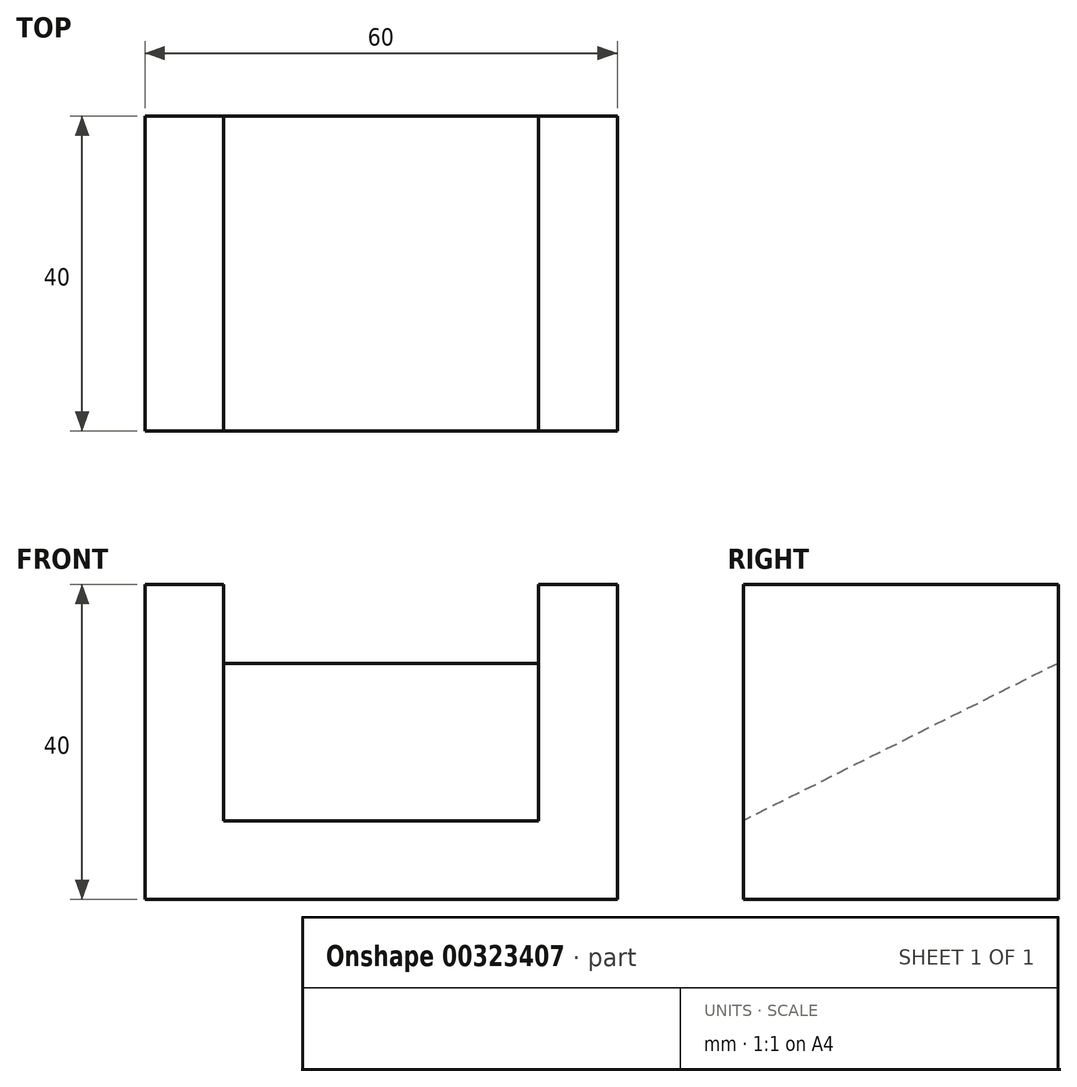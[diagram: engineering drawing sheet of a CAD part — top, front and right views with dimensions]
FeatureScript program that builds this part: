
annotation { "Feature Type Name" : "Feature", "Feature Type Description" : "" }
export const myFeature = defineFeature(function(context is Context, id is Id, definition is map)
    precondition{}
    {
        {
            var Q0;
            Q0=qCreatedBy(makeId("Right.planeOp"),FACE);
            var sketch = newSketch(context, id + "F0", { "sketchPlane" : qUnion([Q0])});
            skLineSegment(sketch, "E0.bottom", {"start": v(0, 0) * mm, "end": v(40, 0) * mm});
            skLineSegment(sketch, "E0.top", {"start": v(0, 40) * mm, "end": v(40, 40) * mm});
            skLineSegment(sketch, "E0.left", {"start": v(0, 0) * mm, "end": v(0, 40) * mm});
            skLineSegment(sketch, "E0.right", {"start": v(40, 0) * mm, "end": v(40, 40) * mm});
            skSolve(sketch);
        }
        {
            var Q0;
            Q0 = qSketchRegion(id + "F0", true);
            extrude(context, id + "F1", {"entities" : qUnion([Q0]), "endBound" : BoundingType.SYMMETRIC, "oppositeDirection" : true, "depth" : 60 * mm});
        }
        {
            var Q0;
            Q0=qCreatedBy(makeId("Right.planeOp"),FACE);
            var sketch = newSketch(context, id + "F2", { "sketchPlane" : qUnion([Q0])});
            skLineSegment(sketch, "E1.0", {"start": v(0, 40) * mm, "end": v(40, 40) * mm});
            skLineSegment(sketch, "E2", {"start": v(0, 40) * mm, "end": v(0, 10) * mm});
            skLineSegment(sketch, "E3", {"start": v(40, 40) * mm, "end": v(40, 30) * mm});
            skLineSegment(sketch, "E4", {"start": v(40, 30) * mm, "end": v(0, 10) * mm});
            skSolve(sketch);
        }
        {
            var Q0;
            Q0 = qSketchRegion(id + "F2", true);
            extrude(context, id + "F3", {"entities" : qUnion([Q0]), "operationType" : NewBodyOperationType.REMOVE, "endBound" : BoundingType.SYMMETRIC, "oppositeDirection" : true, "depth" : 40 * mm});
        }
    });
